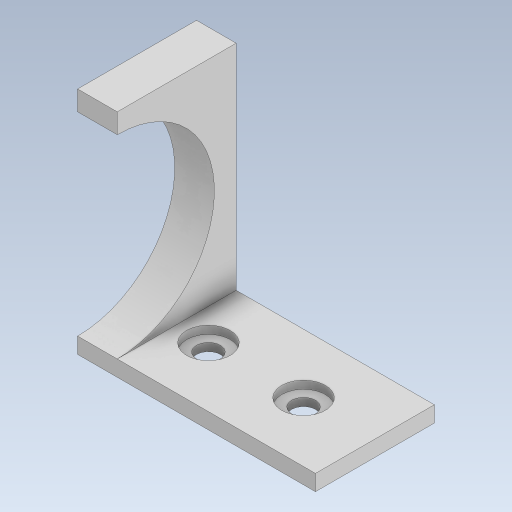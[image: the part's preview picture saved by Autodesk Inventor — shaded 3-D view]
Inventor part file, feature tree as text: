
AUTODESK INVENTOR PART (.ipt)
format: ipt  version: 2023.5 (Build 275446000, 446)  size: 299,520 bytes
history: native  units: in
note: dims shown in document units (in); Inventor stores cm internally (conversion verified against a paired STEP export)
features: extrude x5, sketch x3
ambient origin geometry x8: Origin, YZ Plane, XZ Plane, XY Plane, X Axis, Y Axis, Z Axis, Center Point
bodies: Solid1 (feature_tree)
feature tree (8):
  sketch  "Sketch1"  dims[d0=1.1811in d1=0.5906in]
  extrude  "Extrusion1"  Depth=0.5906in
  extrude  "Extrusion2"  Depth=0.0787in
  extrude  "Extrusion3"  Depth=0.2362in
  extrude  "Extrusion4"  Depth=0.0787in TaperAngle=0.0deg
  extrude  "Extrusion5"  Depth=0.0394in TaperAngle=0.0deg
  sketch  "Sketch2"  dims[d2=0.0787in d3=0.1181in]
  sketch  "Sketch3"  dims[d4=0.2165in d5=0.2362in d6=0.0787in d7=0.0in d8=0.0394in d9=0.0in d10=1.1417in d11=0.0in d13=1.1811in d14=0.0in d15=0.9646in d16=0.4823in d17=0.1181in d18=0.0in]
